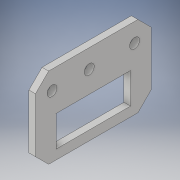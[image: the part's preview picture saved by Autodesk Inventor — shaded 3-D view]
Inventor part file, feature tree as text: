
AUTODESK INVENTOR PART (.ipt)
format: ipt  version: 2017 (Build 210142000, 142)  size: 121,344 bytes
history: native  units: in
note: dims shown in document units (in); Inventor stores cm internally (conversion verified against a paired STEP export)
features: extrude x1, chamfer x1, sketch x1
ambient origin geometry x8: Origin, YZ Plane, XZ Plane, XY Plane, X Axis, Y Axis, Z Axis, Center Point
bodies: Solid1 (feature_tree)
feature tree (3):
  extrude  "Extrusion1"  Depth=1.76in
  chamfer  "Chamfer1"  Distance=0.152in
  sketch  "Sketch1"  dims[d0=1.23in d1=1.76in d2=0.152in d3=0.152in d4=0.152in d5=0.251in d6=0.251in d7=0.286in d8=0.286in d9=0.286in d10=0.47in d11=1.135in d12=0.616in d13=0.3125in d14=0.1in d15=0.0in d16=0.2in d17=0.125in d18=45.0deg]
